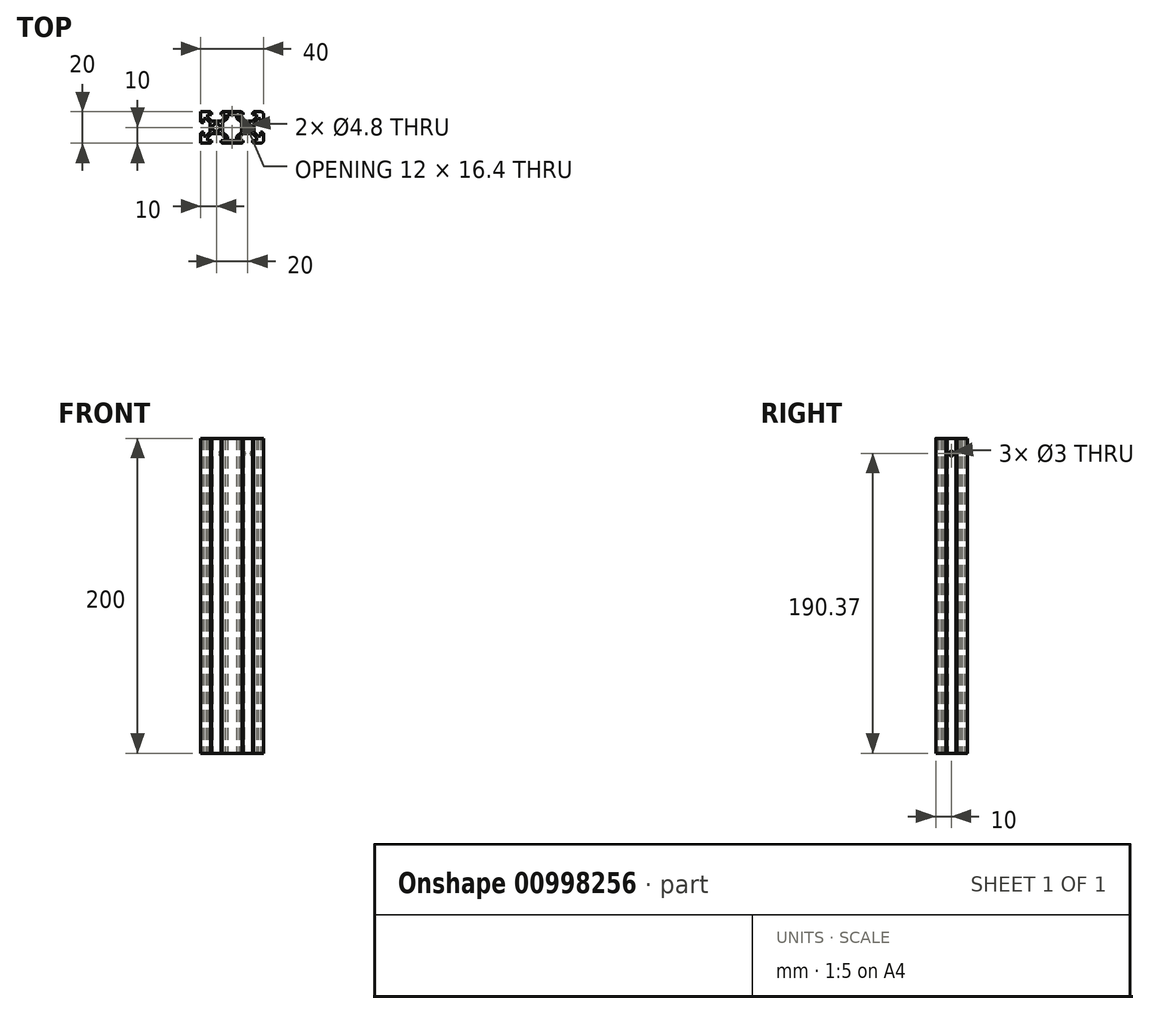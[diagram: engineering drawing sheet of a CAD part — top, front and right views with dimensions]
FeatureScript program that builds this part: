
annotation { "Feature Type Name" : "Feature", "Feature Type Description" : "" }
export const myFeature = defineFeature(function(context is Context, id is Id, definition is map)
    precondition{}
    {
        {
            var Q0;
            Q0=qCreatedBy(makeId("Top.planeOp"),FACE);
            var sketch = newSketch(context, id + "F0", { "sketchPlane" : qUnion([Q0])});
            skLineSegment(sketch, "E0.bottom", {"start": v(10, 10) * mm, "end": v(3.5, 10) * mm});
            skLineSegment(sketch, "E0.top", {"start": v(10, -10) * mm, "end": v(3.5, -10) * mm});
            skLineSegment(sketch, "E0.left", {"start": v(10, 10) * mm, "end": v(10, 3.5) * mm});
            skPoint(sketch, "E0.middle", {"position": v(0, 0) * mm});
            skLineSegment(sketch, "E1", {"start": v(3.5, 10) * mm, "end": v(3.5, 9.5) * mm});
            skLineSegment(sketch, "E2", {"start": v(3.5, 9.5) * mm, "end": v(3, 9.5) * mm});
            skLineSegment(sketch, "E3", {"start": v(3, 9.5) * mm, "end": v(3, 8.2) * mm});
            skLineSegment(sketch, "E4", {"start": v(3, 8.2) * mm, "end": v(5.5, 8.2) * mm});
            skLineSegment(sketch, "E5", {"start": v(5.5, 8.2) * mm, "end": v(5.5, 6.56) * mm});
            skLineSegment(sketch, "E6", {"start": v(5.5, 6.56) * mm, "end": v(2.94, 4) * mm});
            skLineSegment(sketch, "E7", {"start": v(2.94, 4) * mm, "end": v(0, 4) * mm});
            skLineSegment(sketch, "E8", {"start": v(10, 10) * mm, "end": v(0, 0) * mm, "construction": true});
            skLineSegment(sketch, "E9", {"start": v(0, 10) * mm, "end": v(0, -10) * mm, "construction": true});
            skLineSegment(sketch, "E10", {"start": v(10, 0) * mm, "end": v(-10, 0) * mm, "construction": true});
            skLineSegment(sketch, "E11.MirrorCS", {"start": v(-2.94, 4) * mm, "end": v(0, 4) * mm});
            skLineSegment(sketch, "E12.MirrorCS", {"start": v(10, 3.5) * mm, "end": v(9.5, 3.5) * mm});
            skLineSegment(sketch, "E13.MirrorCS", {"start": v(9.5, 3.5) * mm, "end": v(9.5, 3) * mm});
            skLineSegment(sketch, "E14.MirrorCS", {"start": v(8.2, 5.5) * mm, "end": v(6.56, 5.5) * mm});
            skLineSegment(sketch, "E15.MirrorCS", {"start": v(9.5, 3) * mm, "end": v(8.2, 3) * mm});
            skLineSegment(sketch, "E16.MirrorCS", {"start": v(8.2, 3) * mm, "end": v(8.2, 5.5) * mm});
            skLineSegment(sketch, "E17.MirrorCS", {"start": v(6.56, 5.5) * mm, "end": v(4, 2.94) * mm});
            skLineSegment(sketch, "E18.MirrorCS", {"start": v(-3.5, 9.5) * mm, "end": v(-3, 9.5) * mm});
            skLineSegment(sketch, "E19.MirrorCS", {"start": v(-3.5, 10) * mm, "end": v(-3.5, 9.5) * mm});
            skLineSegment(sketch, "E20.MirrorCS", {"start": v(-5.5, 8.2) * mm, "end": v(-5.5, 6.56) * mm});
            skLineSegment(sketch, "E21.MirrorCS", {"start": v(-3, 9.5) * mm, "end": v(-3, 8.2) * mm});
            skLineSegment(sketch, "E22.MirrorCS", {"start": v(-3, 8.2) * mm, "end": v(-5.5, 8.2) * mm});
            skLineSegment(sketch, "E23.MirrorCS", {"start": v(-10, 10) * mm, "end": v(-3.5, 10) * mm});
            skLineSegment(sketch, "E24.MirrorCS", {"start": v(-5.5, 6.56) * mm, "end": v(-2.94, 4) * mm});
            skLineSegment(sketch, "E25.MirrorCS", {"start": v(-3.5, -10) * mm, "end": v(-3.5, -9.5) * mm});
            skLineSegment(sketch, "E26.MirrorCS", {"start": v(-3.5, -9.5) * mm, "end": v(-3, -9.5) * mm});
            skLineSegment(sketch, "E27.MirrorCS", {"start": v(5.5, -8.2) * mm, "end": v(5.5, -6.56) * mm});
            skLineSegment(sketch, "E28.MirrorCS", {"start": v(3, -8.2) * mm, "end": v(5.5, -8.2) * mm});
            skLineSegment(sketch, "E29.MirrorCS", {"start": v(-3, -9.5) * mm, "end": v(-3, -8.2) * mm});
            skLineSegment(sketch, "E30.MirrorCS", {"start": v(3, -9.5) * mm, "end": v(3, -8.2) * mm});
            skLineSegment(sketch, "E31.MirrorCS", {"start": v(10, -3.5) * mm, "end": v(9.5, -3.5) * mm});
            skLineSegment(sketch, "E32.MirrorCS", {"start": v(3.5, -10) * mm, "end": v(3.5, -9.5) * mm});
            skLineSegment(sketch, "E33.MirrorCS", {"start": v(3.5, -9.5) * mm, "end": v(3, -9.5) * mm});
            skLineSegment(sketch, "E34.MirrorCS", {"start": v(9.5, -3.5) * mm, "end": v(9.5, -3) * mm});
            skLineSegment(sketch, "E35.MirrorCS", {"start": v(-3, -8.2) * mm, "end": v(-5.5, -8.2) * mm});
            skLineSegment(sketch, "E36.MirrorCS", {"start": v(-5.5, -8.2) * mm, "end": v(-5.5, -6.56) * mm});
            skLineSegment(sketch, "E37.MirrorCS", {"start": v(8.2, -5.5) * mm, "end": v(6.56, -5.5) * mm});
            skLineSegment(sketch, "E38.MirrorCS", {"start": v(9.5, -3) * mm, "end": v(8.2, -3) * mm});
            skLineSegment(sketch, "E39.MirrorCS", {"start": v(8.2, -3) * mm, "end": v(8.2, -5.5) * mm});
            skLineSegment(sketch, "E40.MirrorCS", {"start": v(6.56, -5.5) * mm, "end": v(4, -2.94) * mm});
            skLineSegment(sketch, "E41.MirrorCS", {"start": v(2.94, -4) * mm, "end": v(0, -4) * mm});
            skLineSegment(sketch, "E42.MirrorCS", {"start": v(-10, -10) * mm, "end": v(-3.5, -10) * mm});
            skLineSegment(sketch, "E43.MirrorCS", {"start": v(5.5, -6.56) * mm, "end": v(2.94, -4) * mm});
            skLineSegment(sketch, "E44.MirrorCS", {"start": v(-5.5, -6.56) * mm, "end": v(-2.94, -4) * mm});
            skLineSegment(sketch, "E45.MirrorCS", {"start": v(-2.94, -4) * mm, "end": v(0, -4) * mm});
            skLineSegment(sketch, "E46", {"start": v(-4, 2.94) * mm, "end": v(-4, -2.94) * mm});
            skLineSegment(sketch, "E47", {"start": v(4, 2.94) * mm, "end": v(4, -2.94) * mm});
            skCircle(sketch, "E48", {"center": v(0, 0) * mm, "radius": 2.4 * mm});
            skLineSegment(sketch, "E49.trimOffspring", {"start": v(-3.5, -10) * mm, "end": v(-10, -10) * mm});
            skLineSegment(sketch, "E50.trimOffspring", {"start": v(10, -3.5) * mm, "end": v(10, -10) * mm});
            skLineSegment(sketch, "E51.trimOffspring", {"start": v(-10, 10) * mm, "end": v(-10, -10) * mm, "construction": true});
            skLineSegment(sketch, "E52.MirrorCS", {"start": v(-16.5, -10) * mm, "end": v(-16.5, -9.5) * mm});
            skLineSegment(sketch, "E53.MirrorCS", {"start": v(-16.5, -9.5) * mm, "end": v(-17, -9.5) * mm});
            skLineSegment(sketch, "E54.MirrorCS", {"start": v(-23.5, -10) * mm, "end": v(-23.5, -9.5) * mm});
            skLineSegment(sketch, "E55.MirrorCS", {"start": v(-23.5, -9.5) * mm, "end": v(-23, -9.5) * mm});
            skLineSegment(sketch, "E56.MirrorCS", {"start": v(-30, 3.5) * mm, "end": v(-29.5, 3.5) * mm});
            skLineSegment(sketch, "E57.MirrorCS", {"start": v(-29.5, 3.5) * mm, "end": v(-29.5, 3) * mm});
            skLineSegment(sketch, "E58.MirrorCS", {"start": v(-29.5, 3) * mm, "end": v(-28.2, 3) * mm});
            skLineSegment(sketch, "E59.MirrorCS", {"start": v(-29.5, -3) * mm, "end": v(-28.2, -3) * mm});
            skLineSegment(sketch, "E60.MirrorCS", {"start": v(-25.5, 8.2) * mm, "end": v(-25.5, 6.56) * mm});
            skLineSegment(sketch, "E61.MirrorCS", {"start": v(-14.5, -8.2) * mm, "end": v(-14.5, -6.56) * mm});
            skLineSegment(sketch, "E62.MirrorCS", {"start": v(-25.5, -8.2) * mm, "end": v(-25.5, -6.56) * mm});
            skLineSegment(sketch, "E63.MirrorCS", {"start": v(-23, 9.5) * mm, "end": v(-23, 8.2) * mm});
            skLineSegment(sketch, "E64.MirrorCS", {"start": v(-16.5, 9.5) * mm, "end": v(-17, 9.5) * mm});
            skLineSegment(sketch, "E65.MirrorCS", {"start": v(-17, -9.5) * mm, "end": v(-17, -8.2) * mm});
            skLineSegment(sketch, "E66.MirrorCS", {"start": v(-23.5, 9.5) * mm, "end": v(-23, 9.5) * mm});
            skLineSegment(sketch, "E67.MirrorCS", {"start": v(-23, -9.5) * mm, "end": v(-23, -8.2) * mm});
            skLineSegment(sketch, "E68.MirrorCS", {"start": v(-23.5, 10) * mm, "end": v(-23.5, 9.5) * mm});
            skLineSegment(sketch, "E69.MirrorCS", {"start": v(-30, -3.5) * mm, "end": v(-29.5, -3.5) * mm});
            skLineSegment(sketch, "E70.MirrorCS", {"start": v(-16.5, 10) * mm, "end": v(-16.5, 9.5) * mm});
            skLineSegment(sketch, "E71.MirrorCS", {"start": v(-29.5, -3.5) * mm, "end": v(-29.5, -3) * mm});
            skLineSegment(sketch, "E72.MirrorCS", {"start": v(-14.5, 8.2) * mm, "end": v(-14.5, 6.56) * mm});
            skLineSegment(sketch, "E73.MirrorCS", {"start": v(-17, 9.5) * mm, "end": v(-17, 8.2) * mm});
            skPoint(sketch, "E74.MirrorP", {"position": v(-20, 0) * mm});
            skLineSegment(sketch, "E75.MirrorCS", {"start": v(-10, -10) * mm, "end": v(-16.5, -10) * mm});
            skLineSegment(sketch, "E76.MirrorCS", {"start": v(-30, -10) * mm, "end": v(-23.5, -10) * mm});
            skLineSegment(sketch, "E77.MirrorCS", {"start": v(-17.06, 4) * mm, "end": v(-20, 4) * mm});
            skLineSegment(sketch, "E78.MirrorCS", {"start": v(-30, 0.07) * mm, "end": v(-10, 0.07) * mm, "construction": true});
            skLineSegment(sketch, "E79.MirrorCS", {"start": v(-16.5, -10) * mm, "end": v(-10, -10) * mm});
            skLineSegment(sketch, "E80.MirrorCS", {"start": v(-30, 10) * mm, "end": v(-20, 0) * mm, "construction": true});
            skLineSegment(sketch, "E81.MirrorCS", {"start": v(-20, 10) * mm, "end": v(-20, -10) * mm, "construction": true});
            skLineSegment(sketch, "E82.MirrorCS", {"start": v(-30, -3.5) * mm, "end": v(-30, -10) * mm});
            skLineSegment(sketch, "E83.MirrorCS", {"start": v(-14.5, 6.56) * mm, "end": v(-17.06, 4) * mm});
            skLineSegment(sketch, "E84.MirrorCS", {"start": v(-22.94, 4) * mm, "end": v(-20, 4) * mm});
            skLineSegment(sketch, "E85.MirrorCS", {"start": v(-28.2, 5.5) * mm, "end": v(-26.56, 5.5) * mm});
            skLineSegment(sketch, "E86.MirrorCS", {"start": v(-28.2, -5.5) * mm, "end": v(-26.56, -5.5) * mm});
            skCircle(sketch, "E87.MirrorC", {"center": v(-20, 0) * mm, "radius": 2.4 * mm});
            skLineSegment(sketch, "E88.MirrorCS", {"start": v(-24, 2.94) * mm, "end": v(-24, -2.94) * mm});
            skLineSegment(sketch, "E89.MirrorCS", {"start": v(-25.5, 6.56) * mm, "end": v(-22.94, 4) * mm});
            skLineSegment(sketch, "E90.MirrorCS", {"start": v(-17.06, -4) * mm, "end": v(-20, -4) * mm});
            skLineSegment(sketch, "E91.MirrorCS", {"start": v(-28.2, 3) * mm, "end": v(-28.2, 5.5) * mm});
            skLineSegment(sketch, "E92.MirrorCS", {"start": v(-23, 8.2) * mm, "end": v(-25.5, 8.2) * mm});
            skLineSegment(sketch, "E93.MirrorCS", {"start": v(-26.56, 5.5) * mm, "end": v(-24, 2.94) * mm});
            skLineSegment(sketch, "E94.MirrorCS", {"start": v(-17, 8.2) * mm, "end": v(-14.5, 8.2) * mm});
            skLineSegment(sketch, "E95.MirrorCS", {"start": v(-28.2, -3) * mm, "end": v(-28.2, -5.5) * mm});
            skLineSegment(sketch, "E96.MirrorCS", {"start": v(-23, -8.2) * mm, "end": v(-25.5, -8.2) * mm});
            skLineSegment(sketch, "E97.MirrorCS", {"start": v(-10, 10) * mm, "end": v(-16.5, 10) * mm});
            skLineSegment(sketch, "E98.MirrorCS", {"start": v(-26.56, -5.5) * mm, "end": v(-24, -2.94) * mm});
            skLineSegment(sketch, "E99.MirrorCS", {"start": v(-17, -8.2) * mm, "end": v(-14.5, -8.2) * mm});
            skLineSegment(sketch, "E100.MirrorCS", {"start": v(-22.94, -4) * mm, "end": v(-20, -4) * mm});
            skLineSegment(sketch, "E101.MirrorCS", {"start": v(-25.5, -6.56) * mm, "end": v(-22.94, -4) * mm});
            skLineSegment(sketch, "E102.MirrorCS", {"start": v(-30, 10) * mm, "end": v(-30, 3.5) * mm});
            skLineSegment(sketch, "E103.MirrorCS", {"start": v(-14.5, -6.56) * mm, "end": v(-17.06, -4) * mm});
            skLineSegment(sketch, "E104.MirrorCS", {"start": v(-30, 10) * mm, "end": v(-23.5, 10) * mm});
            skLineSegment(sketch, "E105", {"start": v(-7, 8.2) * mm, "end": v(-7, 5.94) * mm});
            skLineSegment(sketch, "E106", {"start": v(-4, 2.94) * mm, "end": v(-7, 5.94) * mm});
            skLineSegment(sketch, "E107.MirrorCS", {"start": v(-16, 2.94) * mm, "end": v(-16, -2.94) * mm});
            skLineSegment(sketch, "E108.MirrorCS", {"start": v(-13, 8.2) * mm, "end": v(-13, 5.94) * mm});
            skLineSegment(sketch, "E109.MirrorCS", {"start": v(-16, 2.94) * mm, "end": v(-13, 5.94) * mm});
            skLineSegment(sketch, "E110.MirrorCS", {"start": v(-16, -2.8) * mm, "end": v(-13, -5.8) * mm});
            skLineSegment(sketch, "E111.MirrorCS", {"start": v(-4, -2.8) * mm, "end": v(-7, -5.8) * mm});
            skLineSegment(sketch, "E112.MirrorCS", {"start": v(-7, -8.2) * mm, "end": v(-7, -5.8) * mm});
            skLineSegment(sketch, "E113.MirrorCS", {"start": v(-13, -8.2) * mm, "end": v(-13, -5.8) * mm});
            skLineSegment(sketch, "E114", {"start": v(-13, -8.2) * mm, "end": v(-7, -8.2) * mm});
            skLineSegment(sketch, "E115", {"start": v(-13, 8.2) * mm, "end": v(-7, 8.2) * mm});
            skPoint(sketch, "E116.orphan", {"position": v(-13, 8.34) * mm});
            skPoint(sketch, "E117.orphan", {"position": v(-7, 8.34) * mm});
            skSolve(sketch);
        }
        {
            var Q0;
            Q0=qSketchRegion(id+"F0",true);
            extrude(context, id + "F1", {"entities" : qUnion([Q0]), "depth" : 200 * mm, "offsetDistance" : 25 * mm});
        }
        {
            var Q0;
            Q0=makeQuery(id+"F1.opExtrude","SWEPT_EDGE",EDGE,{"disambiguationData":[OSD([sQuery(id+"F0.wireOp",EDGE,"E0.bottom"),sQuery(id+"F0.wireOp",EDGE,"E0.left")])]});
            var Q1;
            Q1=makeQuery(id+"F1.opExtrude","SWEPT_EDGE",EDGE,{"disambiguationData":[OSD([sQuery(id+"F0.wireOp",EDGE,"E0.top"),sQuery(id+"F0.wireOp",EDGE,"E50.trimOffspring")])]});
            var Q2;
            Q2=makeQuery(id+"F1.opExtrude","SWEPT_EDGE",EDGE,{"disambiguationData":[OSD([sQuery(id+"F0.wireOp",EDGE,"E49.trimOffspring"),sQuery(id+"F0.wireOp",EDGE,"E51.trimOffspring")])]});
            var Q3;
            Q3=makeQuery(id+"F1.opExtrude","SWEPT_EDGE",EDGE,{"disambiguationData":[OSD([sQuery(id+"F0.wireOp",EDGE,"E0.right"),sQuery(id+"F0.wireOp",EDGE,"E23.MirrorCS")])]});
            fillet(context, id + "F2", {"entities" : qUnion([Q0, Q1, Q2, Q3]), "radius" : 2 * mm, "tangentPropagation" : true, "allowEdgeOverflow" : false});
        }
        {
            var Q0;
            Q0=makeQuery(id+"F1.opExtrude","SWEPT_FACE",FACE,{"disambiguationData":[OSD([sQuery(id+"F0.wireOp",EDGE,"E47")])]});
            var sketch = newSketch(context, id + "F3", { "sketchPlane" : qUnion([Q0])});
            skCircle(sketch, "E118", {"center": v(0, 190.37) * mm, "radius": 1.5 * mm});
            skSolve(sketch);
        }
        {
            var Q0;
            Q0=makeQuery(id+"F3.imprint","IMPRINT",FACE,{"disambiguationData":[TD([[makeQuery(id+"F3.imprint","IMPRINT",EDGE,{"derivedFrom":sQuery(id+"F3.wireOp",EDGE,"E118")}),1.0]])]});
            extrude(context, id + "F4", {"entities" : qUnion([Q0]), "operationType" : NewBodyOperationType.REMOVE, "oppositeDirection" : true, "depth" : 25 * mm, "offsetDistance" : 25 * mm});
        }
    });
